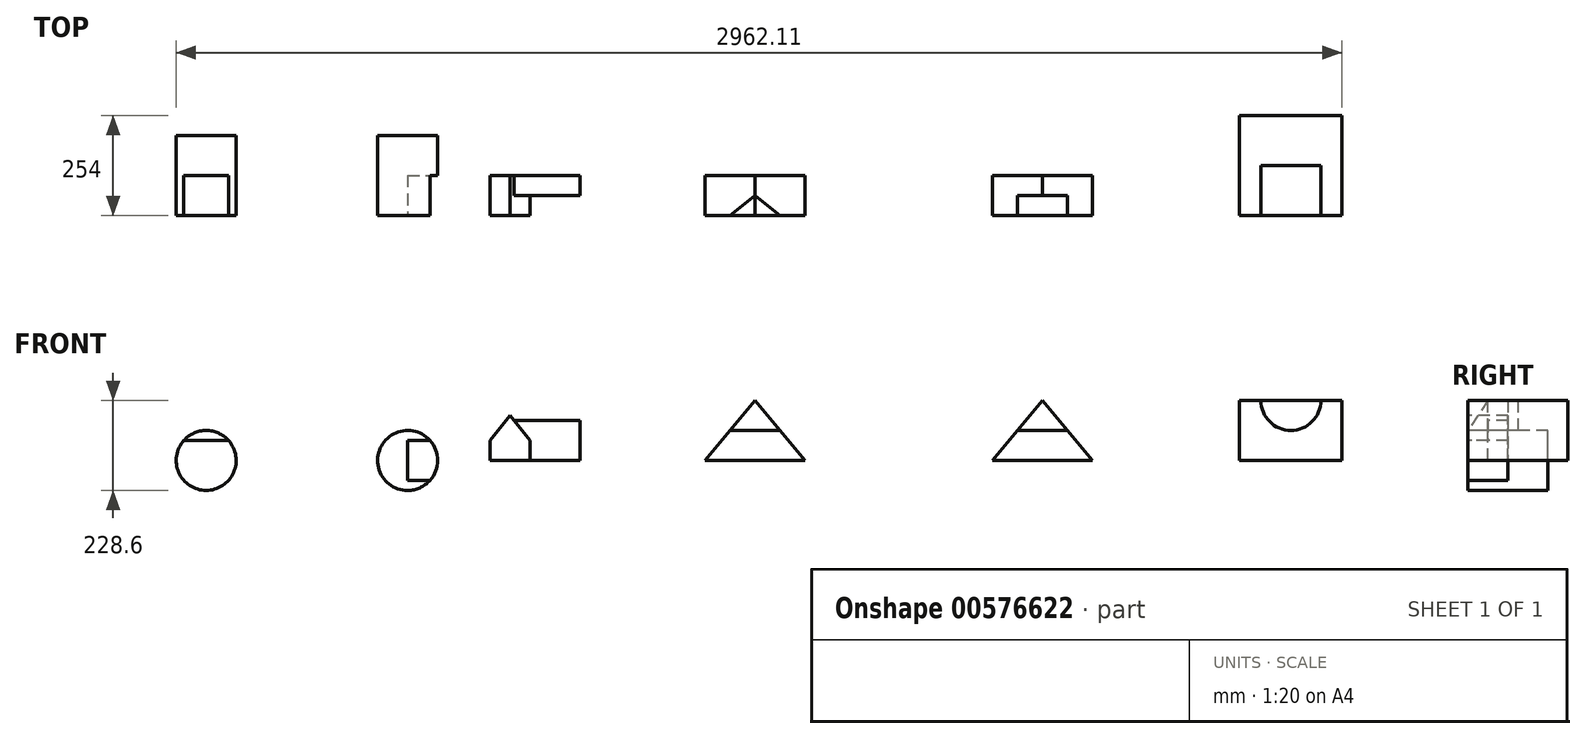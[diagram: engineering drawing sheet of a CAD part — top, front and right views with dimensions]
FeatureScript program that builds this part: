
annotation { "Feature Type Name" : "Feature", "Feature Type Description" : "" }
export const myFeature = defineFeature(function(context is Context, id is Id, definition is map)
    precondition{}
    {
        {
            var Q0;
            Q0=qCreatedBy(makeId("Front.planeOp"),FACE);
            var sketch = newSketch(context, id + "F0", { "sketchPlane" : qUnion([Q0])});
            skLineSegment(sketch, "E0.bottom", {"start": v(147.92, 0) * mm, "end": v(401.92, 0) * mm});
            skLineSegment(sketch, "E0.top", {"start": v(147.92, 152.4) * mm, "end": v(401.92, 152.4) * mm});
            skLineSegment(sketch, "E0.left", {"start": v(147.92, 0) * mm, "end": v(147.92, 152.4) * mm});
            skLineSegment(sketch, "E0.right", {"start": v(401.92, 0) * mm, "end": v(401.92, 152.4) * mm});
            skLineSegment(sketch, "E1", {"start": v(147.92, 152.4) * mm, "end": v(274.92, 152.4) * mm});
            skLineSegment(sketch, "E2", {"start": v(274.92, 152.4) * mm, "end": v(147.92, 0) * mm});
            skLineSegment(sketch, "E3", {"start": v(401.92, 0) * mm, "end": v(274.92, 152.4) * mm});
            skLineSegment(sketch, "E4", {"start": v(147.92, 152.4) * mm, "end": v(147.92, 76.2) * mm});
            skLineSegment(sketch, "E5", {"start": v(211.42, 76.2) * mm, "end": v(338.42, 76.2) * mm});
            skSolve(sketch);
        }
        {
            var Q0;
            {var subQ0=sQuery(id+"F0.wireOp",EDGE,"E0.bottom");Q0=makeQuery(id+"F0.imprint","IMPRINT",FACE,{"disambiguationData":[TD([[makeQuery(id+"F0.imprint","IMPRINT",EDGE,{"derivedFrom":subQ0}),1.0]])]});}
            extrude(context, id + "F1", {"entities" : qUnion([Q0]), "oppositeDirection" : true, "depth" : 101.6 * mm, "offsetDistance" : 25.4 * mm});
        }
        {
            var Q0;
            {var subQ3=sQuery(id+"F0.wireOp",EDGE,"E5");Q0=makeQuery(id+"F0.imprint","IMPRINT",FACE,{"disambiguationData":[TD([[makeQuery(id+"F0.imprint","IMPRINT",EDGE,{"derivedFrom":subQ3}),1.0]])]});}
            extrude(context, id + "F2", {"entities" : qUnion([Q0]), "operationType" : NewBodyOperationType.ADD, "oppositeDirection" : true, "depth" : 101.6 * mm, "offsetDistance" : 25.4 * mm});
        }
        {
            var Q0;
            {var subQ3=sQuery(id+"F0.wireOp",EDGE,"E5");Q0=makeQuery(id+"F0.imprint","IMPRINT",FACE,{"disambiguationData":[TD([[makeQuery(id+"F0.imprint","IMPRINT",EDGE,{"derivedFrom":subQ3}),1.0]])]});}
            extrude(context, id + "F3", {"entities" : qUnion([Q0]), "operationType" : NewBodyOperationType.REMOVE, "oppositeDirection" : true, "depth" : 50.8 * mm, "offsetDistance" : 25.4 * mm});
        }
        {
            var Q0;
            Q0=qCreatedBy(makeId("Front.planeOp"),FACE);
            var sketch = newSketch(context, id + "F4", { "sketchPlane" : qUnion([Q0])});
            skLineSegment(sketch, "E6.bottom", {"start": v(-327.9, 0) * mm, "end": v(-581.9, 0) * mm});
            skLineSegment(sketch, "E7", {"start": v(-581.9, 0) * mm, "end": v(-454.9, 152.4) * mm});
            skLineSegment(sketch, "E8", {"start": v(-454.9, 152.4) * mm, "end": v(-327.9, 0) * mm});
            skLineSegment(sketch, "E9", {"start": v(-454.9, 152.4) * mm, "end": v(-454.9, 76.2) * mm});
            skLineSegment(sketch, "E10", {"start": v(-518.4, 76.2) * mm, "end": v(-391.4, 76.2) * mm});
            skSolve(sketch);
        }
        {
            var Q0;
            Q0 = qSketchRegion(id + "F4", true);
            extrude(context, id + "F5", {"entities" : qUnion([Q0]), "oppositeDirection" : true, "depth" : 101.6 * mm, "offsetDistance" : 25.4 * mm});
        }
        {
            var Q0;
            Q0=makeQuery(id+"F5.opExtrude","CAP_EDGE",EDGE,{"disambiguationData":[OSD([sQuery(id+"F4.wireOp",EDGE,"E6.bottom")])],"isStart":true});
            cPoint(context, id + "F6", {"entities" : qUnion([Q0]), "parameter" : 0.5});
        }
        {
            var Q0;
            Q0=makeQuery(id+"F5.opExtrude","CAP_VERTEX",VERTEX,{"disambiguationData":[OSD([sQuery(id+"F4.wireOp",EDGE,"E7"),sQuery(id+"F4.wireOp",EDGE,"E8"),sQuery(id+"F4.wireOp",EDGE,"E9")])],"isStart":true});
            var Q1;
            Q1=makeQuery(id+"F5.opExtrude","CAP_VERTEX",VERTEX,{"disambiguationData":[OSD([sQuery(id+"F4.wireOp",EDGE,"E7"),sQuery(id+"F4.wireOp",EDGE,"E8"),sQuery(id+"F4.wireOp",EDGE,"E9")])],"isStart":false});
            var Q2;
            Q2 = qCreatedBy(id + "F6" ,VERTEX);
            cPlane(context, id + "F7", {"entities" : qUnion([Q0, Q1, Q2]), "cplaneType" : CPlaneType.THREE_POINT, "offset" : 25.4 * mm, "width" : 152.4 * mm, "height" : 152.4 * mm});
        }
        {
            var Q0;
            Q0=qCreatedBy(id+"F7.planeOp",FACE);
            var sketch = newSketch(context, id + "F8", { "sketchPlane" : qUnion([Q0])});
            skLineSegment(sketch, "E11", {"start": v(0, 0) * mm, "end": v(0, 76.2) * mm});
            skLineSegment(sketch, "E12", {"start": v(0, 76.2) * mm, "end": v(50.8, 152) * mm});
            skLineSegment(sketch, "E13", {"start": v(50.8, 152) * mm, "end": v(0, 152) * mm});
            skLineSegment(sketch, "E14", {"start": v(0, 152) * mm, "end": v(0, 76.2) * mm});
            skSolve(sketch);
        }
        {
            var Q0;
            Q0 = qSketchRegion(id + "F8", true);
            extrude(context, id + "F9", {"entities" : qUnion([Q0]), "operationType" : NewBodyOperationType.REMOVE, "endBound" : BoundingType.SYMMETRIC, "oppositeDirection" : true, "depth" : 127 * mm, "offsetDistance" : 25.4 * mm});
        }
        {
            var Q0;
            Q0=qCreatedBy(makeId("Front.planeOp"),FACE);
            var sketch = newSketch(context, id + "F10", { "sketchPlane" : qUnion([Q0])});
            skLineSegment(sketch, "E15.bottom", {"start": v(-898.97, 0) * mm, "end": v(-1127.57, 0) * mm});
            skLineSegment(sketch, "E15.top", {"start": v(-898.97, 101.6) * mm, "end": v(-1066.6, 101.6) * mm});
            skLineSegment(sketch, "E15.left", {"start": v(-898.97, 0) * mm, "end": v(-898.97, 101.6) * mm});
            skLineSegment(sketch, "E15.right", {"start": v(-1127.57, 0) * mm, "end": v(-1127.57, 50.8) * mm});
            skLineSegment(sketch, "E16", {"start": v(-1127.57, 50.8) * mm, "end": v(-1076.77, 114.3) * mm});
            skLineSegment(sketch, "E17", {"start": v(-1127.57, 0) * mm, "end": v(-1025.97, 0) * mm});
            skLineSegment(sketch, "E18", {"start": v(-1025.97, 0) * mm, "end": v(-1025.97, 50.8) * mm});
            skLineSegment(sketch, "E19", {"start": v(-1025.97, 50.8) * mm, "end": v(-898.97, 50.8) * mm});
            skLineSegment(sketch, "E20", {"start": v(-1076.77, 114.3) * mm, "end": v(-1025.97, 50.8) * mm});
            skSolve(sketch);
        }
        {
            var Q0;
            {var subQ0=sQuery(id+"F10.wireOp",EDGE,"E15.top");Q0=makeQuery(id+"F10.imprint","IMPRINT",FACE,{"disambiguationData":[TD([[makeQuery(id+"F10.imprint","IMPRINT",EDGE,{"derivedFrom":subQ0}),1.0]])]});}
            var Q1;
            Q1=makeQuery(id+"F10.imprint","IMPRINT",FACE,{"disambiguationData":[TD([[makeQuery(id+"F10.imprint","IMPRINT",EDGE,{"derivedFrom":sQuery(id+"F10.wireOp",EDGE,"E15.right")}),-1.0]])]});
            var Q2;
            {var subQ0=sQuery(id+"F10.wireOp",EDGE,"E15.bottom");Q2=makeQuery(id+"F10.imprint","IMPRINT",FACE,{"disambiguationData":[TD([[makeQuery(id+"F10.imprint","IMPRINT",EDGE,{"derivedFrom":subQ0}),-1.0]])]});}
            extrude(context, id + "F11", {"entities" : qUnion([Q0, Q1, Q2]), "oppositeDirection" : true, "depth" : 101.6 * mm, "offsetDistance" : 25.4 * mm});
        }
        {
            var Q0;
            {var subQ0=sQuery(id+"F10.wireOp",EDGE,"E15.top");Q0=makeQuery(id+"F10.imprint","IMPRINT",FACE,{"disambiguationData":[TD([[makeQuery(id+"F10.imprint","IMPRINT",EDGE,{"derivedFrom":subQ0}),1.0]])]});}
            var Q1;
            {var subQ0=sQuery(id+"F10.wireOp",EDGE,"E15.bottom");Q1=makeQuery(id+"F10.imprint","IMPRINT",FACE,{"disambiguationData":[TD([[makeQuery(id+"F10.imprint","IMPRINT",EDGE,{"derivedFrom":subQ0}),-1.0]])]});}
            extrude(context, id + "F12", {"entities" : qUnion([Q0, Q1]), "operationType" : NewBodyOperationType.REMOVE, "oppositeDirection" : true, "depth" : 50.8 * mm, "offsetDistance" : 25.4 * mm});
        }
        {
            var Q0;
            Q0=qCreatedBy(makeId("Front.planeOp"),FACE);
            var sketch = newSketch(context, id + "F13", { "sketchPlane" : qUnion([Q0])});
            skCircle(sketch, "E21", {"center": v(-1849.11, 0) * mm, "radius": 76.2 * mm});
            skLineSegment(sketch, "E22", {"start": v(-1849.11, 50.8) * mm, "end": v(-1905.9, 50.8) * mm});
            skLineSegment(sketch, "E23", {"start": v(-1849.11, 50.8) * mm, "end": v(-1792.32, 50.8) * mm});
            skSolve(sketch);
        }
        {
            var Q0;
            {var subQ0=sQuery(id+"F13.wireOp",EDGE,"E22");Q0=makeQuery(id+"F13.imprint","IMPRINT",FACE,{"disambiguationData":[TD([[makeQuery(id+"F13.imprint","IMPRINT",EDGE,{"derivedFrom":subQ0}),1.0]])]});}
            var Q1;
            {var subQ0=sQuery(id+"F13.wireOp",EDGE,"E22");Q1=makeQuery(id+"F13.imprint","IMPRINT",FACE,{"disambiguationData":[TD([[makeQuery(id+"F13.imprint","IMPRINT",EDGE,{"derivedFrom":subQ0}),-1.0]])]});}
            extrude(context, id + "F14", {"entities" : qUnion([Q0, Q1]), "oppositeDirection" : true, "depth" : 203.2 * mm, "offsetDistance" : 25.4 * mm});
        }
        {
            var Q0;
            {var subQ0=sQuery(id+"F13.wireOp",EDGE,"E22");Q0=makeQuery(id+"F13.imprint","IMPRINT",FACE,{"disambiguationData":[TD([[makeQuery(id+"F13.imprint","IMPRINT",EDGE,{"derivedFrom":subQ0}),-1.0]])]});}
            extrude(context, id + "F15", {"entities" : qUnion([Q0]), "operationType" : NewBodyOperationType.REMOVE, "oppositeDirection" : true, "depth" : 101.6 * mm, "offsetDistance" : 25.4 * mm});
        }
        {
            var Q0;
            Q0=qCreatedBy(makeId("Front.planeOp"),FACE);
            var sketch = newSketch(context, id + "F16", { "sketchPlane" : qUnion([Q0])});
            skCircle(sketch, "E24", {"center": v(-1337.19, 0) * mm, "radius": 76.2 * mm});
            skLineSegment(sketch, "E25", {"start": v(-1337.19, 0) * mm, "end": v(-1337.19, 50.8) * mm});
            skLineSegment(sketch, "E26", {"start": v(-1337.19, 0) * mm, "end": v(-1337.19, -50.8) * mm});
            skLineSegment(sketch, "E27", {"start": v(-1337.19, -50.8) * mm, "end": v(-1280.4, -50.8) * mm});
            skLineSegment(sketch, "E28", {"start": v(-1337.19, 50.8) * mm, "end": v(-1280.4, 50.8) * mm});
            skSolve(sketch);
        }
        {
            var Q0;
            Q0 = qSketchRegion(id + "F16", true);
            extrude(context, id + "F17", {"entities" : qUnion([Q0]), "oppositeDirection" : true, "depth" : 203.2 * mm, "offsetDistance" : 25.4 * mm});
        }
        {
            var Q0;
            Q0=makeQuery(id+"F16.imprint","IMPRINT",FACE,{"disambiguationData":[TD([[makeQuery(id+"F16.imprint","IMPRINT",EDGE,{"derivedFrom":sQuery(id+"F16.wireOp",EDGE,"E25")}),-1.0]])]});
            extrude(context, id + "F18", {"entities" : qUnion([Q0]), "operationType" : NewBodyOperationType.REMOVE, "oppositeDirection" : true, "depth" : 101.6 * mm, "offsetDistance" : 25.4 * mm});
        }
        {
            var Q0;
            Q0=qCreatedBy(makeId("Front.planeOp"),FACE);
            var sketch = newSketch(context, id + "F19", { "sketchPlane" : qUnion([Q0])});
            skLineSegment(sketch, "E29.bottom", {"start": v(776.49, 0) * mm, "end": v(1036.8, 0) * mm});
            skLineSegment(sketch, "E29.top", {"start": v(776.49, 152.4) * mm, "end": v(1036.8, 152.4) * mm});
            skLineSegment(sketch, "E29.left", {"start": v(776.49, 0) * mm, "end": v(776.49, 152.4) * mm});
            skLineSegment(sketch, "E29.right", {"start": v(1036.8, 0) * mm, "end": v(1036.8, 152.4) * mm});
            skLineSegment(sketch, "E30", {"start": v(776.49, 152.4) * mm, "end": v(827.29, 152.4) * mm});
            skLineSegment(sketch, "E31", {"start": v(1036.8, 152.4) * mm, "end": v(986, 152.4) * mm});
            skLineSegment(sketch, "E32", {"start": v(776.49, 152.4) * mm, "end": v(906.65, 152.4) * mm});
            skArc(sketch, "E33", {"start": v(830.45, 152.4) * mm, "mid": v(906.65, 76.2) * mm, "end": v(982.85, 152.4) * mm});
            skSolve(sketch);
        }
        {
            var Q0;
            Q0 = qSketchRegion(id + "F19", true);
            extrude(context, id + "F20", {"entities" : qUnion([Q0]), "oppositeDirection" : true, "depth" : 254 * mm, "offsetDistance" : 25.4 * mm});
        }
        {
            var Q0;
            {var subQ3=sQuery(id+"F19.wireOp",EDGE,"E33");Q0=makeQuery(id+"F19.imprint","IMPRINT",FACE,{"disambiguationData":[TD([[makeQuery(id+"F19.imprint","IMPRINT",EDGE,{"derivedFrom":subQ3}),1.0]])]});}
            extrude(context, id + "F21", {"entities" : qUnion([Q0]), "operationType" : NewBodyOperationType.REMOVE, "oppositeDirection" : true, "depth" : 127 * mm, "offsetDistance" : 25.4 * mm});
        }
    });
